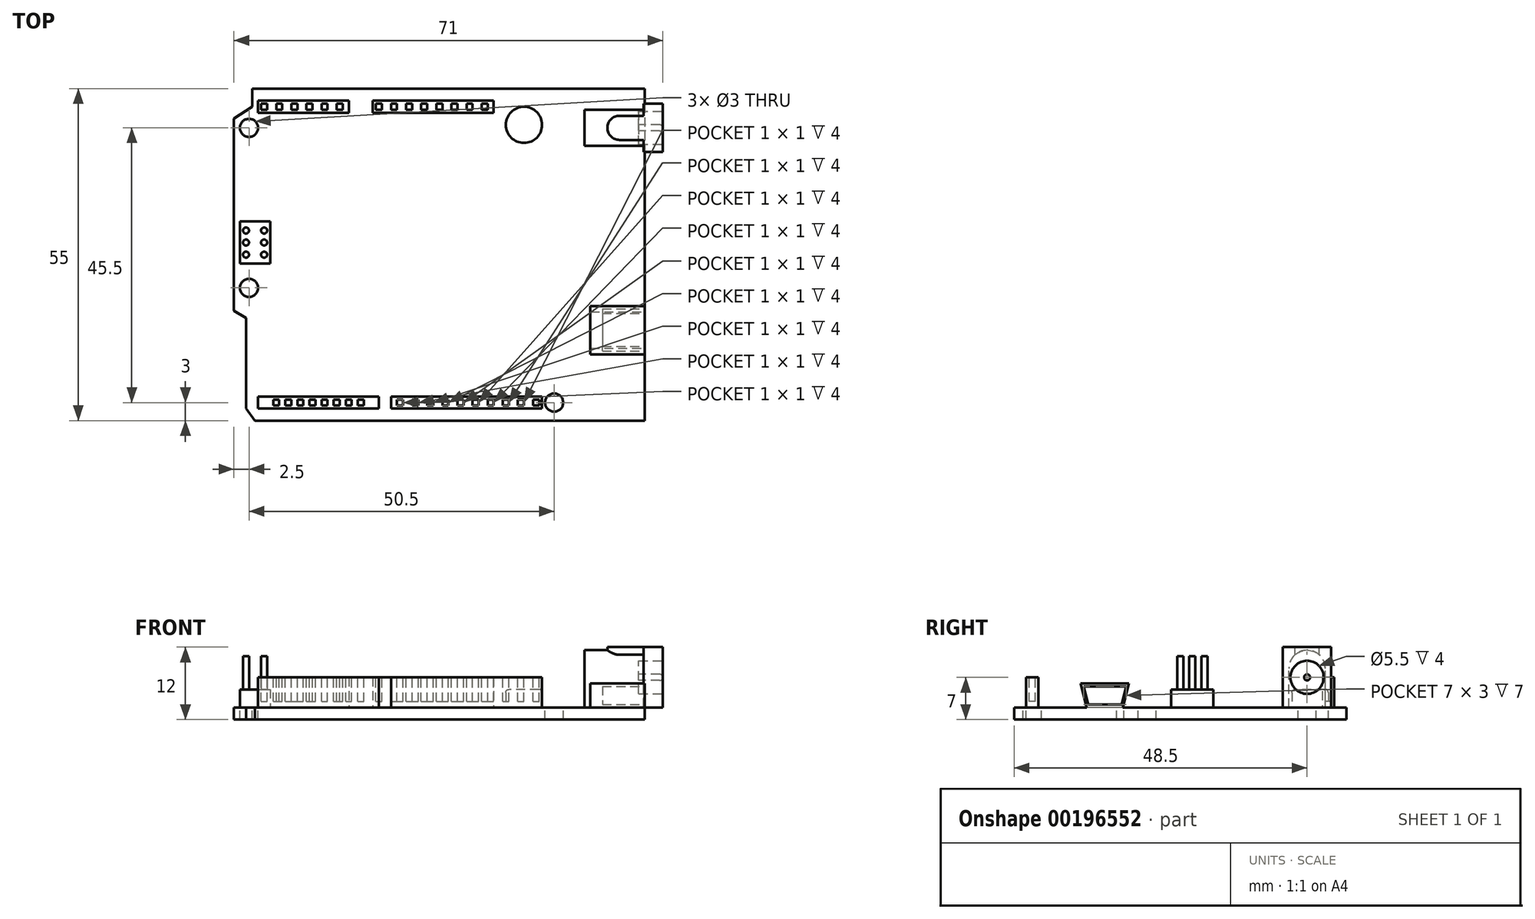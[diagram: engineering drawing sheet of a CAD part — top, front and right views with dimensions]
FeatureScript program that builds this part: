
annotation { "Feature Type Name" : "Feature", "Feature Type Description" : "" }
export const myFeature = defineFeature(function(context is Context, id is Id, definition is map)
    precondition{}
    {
        {
            var Q0;
            Q0=qCreatedBy(makeId("Top.planeOp"),FACE);
            var sketch = newSketch(context, id + "F0", { "sketchPlane" : qUnion([Q0])});
            skLineSegment(sketch, "E0.bottom", {"start": v(-34, 55) * mm, "end": v(34, 55) * mm});
            skLineSegment(sketch, "E0.top", {"start": v(-34, 0) * mm, "end": v(34, 0) * mm});
            skLineSegment(sketch, "E0.left", {"start": v(-34, 55) * mm, "end": v(-34, 0) * mm});
            skLineSegment(sketch, "E0.right", {"start": v(34, 55) * mm, "end": v(34, 0) * mm});
            skSolve(sketch);
        }
        {
            var Q0;
            Q0 = qSketchRegion(id + "F0", true);
            extrude(context, id + "F1", {"entities" : qUnion([Q0]), "depth" : 2 * mm});
        }
        {
            var Q0;
            Q0=makeQuery(id+"F1.opExtrude","CAP_FACE",FACE,{"disambiguationData":[OSD([sQuery(id+"F0.wireOp",EDGE,"E0.bottom"),sQuery(id+"F0.wireOp",EDGE,"E0.top"),sQuery(id+"F0.wireOp",EDGE,"E0.left"),sQuery(id+"F0.wireOp",EDGE,"E0.right")])],"isStart":false});
            var sketch = newSketch(context, id + "F2", { "sketchPlane" : qUnion([Q0])});
            skLineSegment(sketch, "E1.bottom", {"start": v(-34, 17) * mm, "end": v(-32, 17) * mm});
            skLineSegment(sketch, "E1.top", {"start": v(-34, 0) * mm, "end": v(-32, 0) * mm});
            skLineSegment(sketch, "E1.left", {"start": v(-34, 17) * mm, "end": v(-34, 0) * mm});
            skLineSegment(sketch, "E1.right", {"start": v(-32, 17) * mm, "end": v(-32, 0) * mm});
            skSolve(sketch);
        }
        {
            var Q0;
            Q0 = qSketchRegion(id + "F2", true);
            extrude(context, id + "F3", {"entities" : qUnion([Q0]), "operationType" : NewBodyOperationType.REMOVE, "endBound" : BoundingType.UP_TO_NEXT, "oppositeDirection" : true, "depth" : 25 * mm});
        }
        {
            var Q0;
            Q0=makeQuery(id+"F1.opExtrude","CAP_FACE",FACE,{"disambiguationData":[OSD([sQuery(id+"F0.wireOp",EDGE,"E0.bottom"),sQuery(id+"F0.wireOp",EDGE,"E0.top"),sQuery(id+"F0.wireOp",EDGE,"E0.left"),sQuery(id+"F0.wireOp",EDGE,"E0.right")])],"isStart":false});
            var sketch = newSketch(context, id + "F4", { "sketchPlane" : qUnion([Q0])});
            skLineSegment(sketch, "E2", {"start": v(-32, 2) * mm, "end": v(-30.5, 0) * mm});
            skLineSegment(sketch, "E3", {"start": v(-30.5, 0) * mm, "end": v(-32, 0) * mm});
            skLineSegment(sketch, "E4", {"start": v(-32, 0) * mm, "end": v(-32, 2) * mm});
            skSolve(sketch);
        }
        {
            var Q0;
            Q0 = qSketchRegion(id + "F4", true);
            extrude(context, id + "F5", {"entities" : qUnion([Q0]), "operationType" : NewBodyOperationType.REMOVE, "endBound" : BoundingType.UP_TO_NEXT, "oppositeDirection" : true, "depth" : 25 * mm});
        }
        {
            var Q0;
            Q0=makeQuery(id+"F1.opExtrude","CAP_FACE",FACE,{"disambiguationData":[OSD([sQuery(id+"F0.wireOp",EDGE,"E0.bottom"),sQuery(id+"F0.wireOp",EDGE,"E0.top"),sQuery(id+"F0.wireOp",EDGE,"E0.left"),sQuery(id+"F0.wireOp",EDGE,"E0.right")])],"isStart":false});
            var sketch = newSketch(context, id + "F6", { "sketchPlane" : qUnion([Q0])});
            skLineSegment(sketch, "E5", {"start": v(-34, 17) * mm, "end": v(-34, 18.2) * mm});
            skLineSegment(sketch, "E6", {"start": v(-34, 18.2) * mm, "end": v(-32, 17) * mm});
            skLineSegment(sketch, "E7", {"start": v(-32, 17) * mm, "end": v(-34, 17) * mm});
            skSolve(sketch);
        }
        {
            var Q0;
            Q0 = qSketchRegion(id + "F6", true);
            extrude(context, id + "F7", {"entities" : qUnion([Q0]), "operationType" : NewBodyOperationType.REMOVE, "endBound" : BoundingType.UP_TO_NEXT, "oppositeDirection" : true, "depth" : 25 * mm});
        }
        {
            var Q0;
            Q0=makeQuery(id+"F1.opExtrude","CAP_FACE",FACE,{"disambiguationData":[OSD([sQuery(id+"F0.wireOp",EDGE,"E0.bottom"),sQuery(id+"F0.wireOp",EDGE,"E0.top"),sQuery(id+"F0.wireOp",EDGE,"E0.left"),sQuery(id+"F0.wireOp",EDGE,"E0.right")])],"isStart":false});
            var sketch = newSketch(context, id + "F8", { "sketchPlane" : qUnion([Q0])});
            skLineSegment(sketch, "E8", {"start": v(-34, 50) * mm, "end": v(-34, 55) * mm});
            skLineSegment(sketch, "E9", {"start": v(-34, 55) * mm, "end": v(-31, 55) * mm});
            skLineSegment(sketch, "E10", {"start": v(-31, 55) * mm, "end": v(-31, 52) * mm});
            skLineSegment(sketch, "E11", {"start": v(-31, 52) * mm, "end": v(-34, 50) * mm});
            skSolve(sketch);
        }
        {
            var Q0;
            Q0 = qSketchRegion(id + "F8", true);
            extrude(context, id + "F9", {"entities" : qUnion([Q0]), "operationType" : NewBodyOperationType.REMOVE, "endBound" : BoundingType.UP_TO_NEXT, "oppositeDirection" : true, "depth" : 25 * mm});
        }
        {
            var Q0;
            Q0=makeQuery(id+"F1.opExtrude","CAP_FACE",FACE,{"disambiguationData":[OSD([sQuery(id+"F0.wireOp",EDGE,"E0.bottom"),sQuery(id+"F0.wireOp",EDGE,"E0.top"),sQuery(id+"F0.wireOp",EDGE,"E0.left"),sQuery(id+"F0.wireOp",EDGE,"E0.right")])],"isStart":false});
            var sketch = newSketch(context, id + "F10", { "sketchPlane" : qUnion([Q0])});
            skCircle(sketch, "E12", {"center": v(-31.5, 48.5) * mm, "radius": 1.5 * mm});
            skCircle(sketch, "E13", {"center": v(-31.5, 22) * mm, "radius": 1.5 * mm});
            skSolve(sketch);
        }
        {
            var Q0;
            Q0 = qSketchRegion(id + "F10", true);
            extrude(context, id + "F11", {"entities" : qUnion([Q0]), "operationType" : NewBodyOperationType.REMOVE, "endBound" : BoundingType.UP_TO_NEXT, "oppositeDirection" : true, "depth" : 25 * mm});
        }
        {
            var Q0;
            Q0=makeQuery(id+"F1.opExtrude","CAP_FACE",FACE,{"disambiguationData":[OSD([sQuery(id+"F0.wireOp",EDGE,"E0.bottom"),sQuery(id+"F0.wireOp",EDGE,"E0.top"),sQuery(id+"F0.wireOp",EDGE,"E0.left"),sQuery(id+"F0.wireOp",EDGE,"E0.right")])],"isStart":false});
            var sketch = newSketch(context, id + "F12", { "sketchPlane" : qUnion([Q0])});
            skCircle(sketch, "E14", {"center": v(19, 3) * mm, "radius": 1.5 * mm});
            skSolve(sketch);
        }
        {
            var Q0;
            Q0 = qSketchRegion(id + "F12", true);
            extrude(context, id + "F13", {"entities" : qUnion([Q0]), "operationType" : NewBodyOperationType.REMOVE, "endBound" : BoundingType.UP_TO_NEXT, "oppositeDirection" : true, "depth" : 25 * mm});
        }
        {
            var Q0;
            Q0=makeQuery(id+"F1.opExtrude","CAP_FACE",FACE,{"disambiguationData":[OSD([sQuery(id+"F0.wireOp",EDGE,"E0.bottom"),sQuery(id+"F0.wireOp",EDGE,"E0.top"),sQuery(id+"F0.wireOp",EDGE,"E0.left"),sQuery(id+"F0.wireOp",EDGE,"E0.right")])],"isStart":false});
            var sketch = newSketch(context, id + "F14", { "sketchPlane" : qUnion([Q0])});
            skLineSegment(sketch, "E15.bottom", {"start": v(-30, 53) * mm, "end": v(-15, 53) * mm});
            skLineSegment(sketch, "E15.top", {"start": v(-30, 51) * mm, "end": v(-15, 51) * mm});
            skLineSegment(sketch, "E15.left", {"start": v(-30, 53) * mm, "end": v(-30, 51) * mm});
            skLineSegment(sketch, "E15.right", {"start": v(-15, 53) * mm, "end": v(-15, 51) * mm});
            skSolve(sketch);
        }
        {
            var Q0;
            Q0 = qSketchRegion(id + "F14", true);
            extrude(context, id + "F15", {"entities" : qUnion([Q0]), "operationType" : NewBodyOperationType.ADD, "depth" : 5 * mm});
        }
        {
            var Q0;
            Q0=makeQuery(id+"F15.opExtrude","CAP_FACE",FACE,{"disambiguationData":[OSD([sQuery(id+"F14.wireOp",EDGE,"E15.bottom"),sQuery(id+"F14.wireOp",EDGE,"E15.top"),sQuery(id+"F14.wireOp",EDGE,"E15.left"),sQuery(id+"F14.wireOp",EDGE,"E15.right")])],"isStart":false});
            var sketch = newSketch(context, id + "F16", { "sketchPlane" : qUnion([Q0])});
            skPoint(sketch, "E16.oppositeSnap0", {"position": v(-30, 52) * mm});
            skLineSegment(sketch, "E17.bottom", {"start": v(-29.5, 52.5) * mm, "end": v(-28.5, 52.5) * mm});
            skLineSegment(sketch, "E17.top", {"start": v(-29.5, 51.5) * mm, "end": v(-28.5, 51.5) * mm});
            skLineSegment(sketch, "E17.left", {"start": v(-29.5, 52.5) * mm, "end": v(-29.5, 51.5) * mm});
            skLineSegment(sketch, "E17.right", {"start": v(-28.5, 52.5) * mm, "end": v(-28.5, 51.5) * mm});
            skSolve(sketch);
        }
        {
            var Q0;
            Q0 = qSketchRegion(id + "F16", true);
            extrude(context, id + "F17", {"entities" : qUnion([Q0]), "operationType" : NewBodyOperationType.REMOVE, "oppositeDirection" : true, "depth" : 4 * mm});
        }
        {
            var Q0;
            Q0=makeQuery(id+"F15.opExtrude","CAP_FACE",FACE,{"disambiguationData":[OSD([sQuery(id+"F14.wireOp",EDGE,"E15.bottom"),sQuery(id+"F14.wireOp",EDGE,"E15.top"),sQuery(id+"F14.wireOp",EDGE,"E15.left"),sQuery(id+"F14.wireOp",EDGE,"E15.right")])],"isStart":false});
            var sketch = newSketch(context, id + "F18", { "sketchPlane" : qUnion([Q0])});
            skLineSegment(sketch, "E18.bottom", {"start": v(-27, 52.5) * mm, "end": v(-26, 52.5) * mm});
            skLineSegment(sketch, "E18.top", {"start": v(-27, 51.5) * mm, "end": v(-26, 51.5) * mm});
            skLineSegment(sketch, "E18.left", {"start": v(-27, 52.5) * mm, "end": v(-27, 51.5) * mm});
            skLineSegment(sketch, "E18.right", {"start": v(-26, 52.5) * mm, "end": v(-26, 51.5) * mm});
            skLineSegment(sketch, "E19.bottom", {"start": v(-24.5, 52.5) * mm, "end": v(-23.5, 52.5) * mm});
            skLineSegment(sketch, "E19.top", {"start": v(-24.5, 51.5) * mm, "end": v(-23.5, 51.5) * mm});
            skLineSegment(sketch, "E19.left", {"start": v(-24.5, 52.5) * mm, "end": v(-24.5, 51.5) * mm});
            skLineSegment(sketch, "E19.right", {"start": v(-23.5, 52.5) * mm, "end": v(-23.5, 51.5) * mm});
            skLineSegment(sketch, "E20.bottom", {"start": v(-22, 52.5) * mm, "end": v(-21, 52.5) * mm});
            skLineSegment(sketch, "E20.top", {"start": v(-22, 51.5) * mm, "end": v(-21, 51.5) * mm});
            skLineSegment(sketch, "E20.left", {"start": v(-22, 52.5) * mm, "end": v(-22, 51.5) * mm});
            skLineSegment(sketch, "E20.right", {"start": v(-21, 52.5) * mm, "end": v(-21, 51.5) * mm});
            skLineSegment(sketch, "E21.bottom", {"start": v(-19.5, 52.5) * mm, "end": v(-18.5, 52.5) * mm});
            skLineSegment(sketch, "E21.top", {"start": v(-19.5, 51.5) * mm, "end": v(-18.5, 51.5) * mm});
            skLineSegment(sketch, "E21.left", {"start": v(-19.5, 52.5) * mm, "end": v(-19.5, 51.5) * mm});
            skLineSegment(sketch, "E21.right", {"start": v(-18.5, 52.5) * mm, "end": v(-18.5, 51.5) * mm});
            skLineSegment(sketch, "E22.bottom", {"start": v(-17, 52.5) * mm, "end": v(-16, 52.5) * mm});
            skLineSegment(sketch, "E22.top", {"start": v(-17, 51.5) * mm, "end": v(-16, 51.5) * mm});
            skLineSegment(sketch, "E22.left", {"start": v(-17, 52.5) * mm, "end": v(-17, 51.5) * mm});
            skLineSegment(sketch, "E22.right", {"start": v(-16, 52.5) * mm, "end": v(-16, 51.5) * mm});
            skSolve(sketch);
        }
        {
            var Q0;
            Q0 = qSketchRegion(id + "F18", true);
            extrude(context, id + "F19", {"entities" : qUnion([Q0]), "operationType" : NewBodyOperationType.REMOVE, "oppositeDirection" : true, "depth" : 4 * mm});
        }
        {
            var Q0;
            Q0=makeQuery(id+"F1.opExtrude","CAP_FACE",FACE,{"disambiguationData":[OSD([sQuery(id+"F0.wireOp",EDGE,"E0.bottom"),sQuery(id+"F0.wireOp",EDGE,"E0.top"),sQuery(id+"F0.wireOp",EDGE,"E0.left"),sQuery(id+"F0.wireOp",EDGE,"E0.right")])],"isStart":false});
            var sketch = newSketch(context, id + "F20", { "sketchPlane" : qUnion([Q0])});
            skLineSegment(sketch, "E23.bottom", {"start": v(-11, 53) * mm, "end": v(9, 53) * mm});
            skLineSegment(sketch, "E23.top", {"start": v(-11, 51) * mm, "end": v(9, 51) * mm});
            skLineSegment(sketch, "E23.left", {"start": v(-11, 53) * mm, "end": v(-11, 51) * mm});
            skLineSegment(sketch, "E23.right", {"start": v(9, 53) * mm, "end": v(9, 51) * mm});
            skSolve(sketch);
        }
        {
            var Q0;
            Q0 = qSketchRegion(id + "F20", true);
            extrude(context, id + "F21", {"entities" : qUnion([Q0]), "operationType" : NewBodyOperationType.ADD, "depth" : 5 * mm});
        }
        {
            var Q0;
            Q0=makeQuery(id+"F21.opExtrude","CAP_FACE",FACE,{"disambiguationData":[OSD([sQuery(id+"F20.wireOp",EDGE,"E23.bottom"),sQuery(id+"F20.wireOp",EDGE,"E23.top"),sQuery(id+"F20.wireOp",EDGE,"E23.left"),sQuery(id+"F20.wireOp",EDGE,"E23.right")])],"isStart":false});
            var sketch = newSketch(context, id + "F22", { "sketchPlane" : qUnion([Q0])});
            skLineSegment(sketch, "E24.bottom", {"start": v(-10.5, 52.5) * mm, "end": v(-9.5, 52.5) * mm});
            skLineSegment(sketch, "E24.top", {"start": v(-10.5, 51.5) * mm, "end": v(-9.5, 51.5) * mm});
            skLineSegment(sketch, "E24.left", {"start": v(-10.5, 52.5) * mm, "end": v(-10.5, 51.5) * mm});
            skLineSegment(sketch, "E24.right", {"start": v(-9.5, 52.5) * mm, "end": v(-9.5, 51.5) * mm});
            skLineSegment(sketch, "E25.bottom", {"start": v(-8, 52.5) * mm, "end": v(-7, 52.5) * mm});
            skLineSegment(sketch, "E25.top", {"start": v(-8, 51.5) * mm, "end": v(-7, 51.5) * mm});
            skLineSegment(sketch, "E25.left", {"start": v(-8, 52.5) * mm, "end": v(-8, 51.5) * mm});
            skLineSegment(sketch, "E25.right", {"start": v(-7, 52.5) * mm, "end": v(-7, 51.5) * mm});
            skLineSegment(sketch, "E26.bottom", {"start": v(-5.5, 52.5) * mm, "end": v(-4.5, 52.5) * mm});
            skLineSegment(sketch, "E26.top", {"start": v(-5.5, 51.5) * mm, "end": v(-4.5, 51.5) * mm});
            skLineSegment(sketch, "E26.left", {"start": v(-5.5, 52.5) * mm, "end": v(-5.5, 51.5) * mm});
            skLineSegment(sketch, "E26.right", {"start": v(-4.5, 52.5) * mm, "end": v(-4.5, 51.5) * mm});
            skLineSegment(sketch, "E27.bottom", {"start": v(-3, 52.5) * mm, "end": v(-2, 52.5) * mm});
            skLineSegment(sketch, "E27.top", {"start": v(-3, 51.5) * mm, "end": v(-2, 51.5) * mm});
            skLineSegment(sketch, "E27.left", {"start": v(-3, 52.5) * mm, "end": v(-3, 51.5) * mm});
            skLineSegment(sketch, "E27.right", {"start": v(-2, 52.5) * mm, "end": v(-2, 51.5) * mm});
            skLineSegment(sketch, "E28.bottom", {"start": v(-0.5, 52.5) * mm, "end": v(0.5, 52.5) * mm});
            skLineSegment(sketch, "E28.top", {"start": v(-0.5, 51.5) * mm, "end": v(0.5, 51.5) * mm});
            skLineSegment(sketch, "E28.left", {"start": v(-0.5, 52.5) * mm, "end": v(-0.5, 51.5) * mm});
            skLineSegment(sketch, "E28.right", {"start": v(0.5, 52.5) * mm, "end": v(0.5, 51.5) * mm});
            skLineSegment(sketch, "E29.bottom", {"start": v(2, 52.5) * mm, "end": v(3, 52.5) * mm});
            skLineSegment(sketch, "E29.top", {"start": v(2, 51.5) * mm, "end": v(3, 51.5) * mm});
            skLineSegment(sketch, "E29.left", {"start": v(2, 52.5) * mm, "end": v(2, 51.5) * mm});
            skLineSegment(sketch, "E29.right", {"start": v(3, 52.5) * mm, "end": v(3, 51.5) * mm});
            skLineSegment(sketch, "E30.bottom", {"start": v(4.5, 52.5) * mm, "end": v(5.5, 52.5) * mm});
            skLineSegment(sketch, "E30.top", {"start": v(4.5, 51.5) * mm, "end": v(5.5, 51.5) * mm});
            skLineSegment(sketch, "E30.left", {"start": v(4.5, 52.5) * mm, "end": v(4.5, 51.5) * mm});
            skLineSegment(sketch, "E30.right", {"start": v(5.5, 52.5) * mm, "end": v(5.5, 51.5) * mm});
            skLineSegment(sketch, "E31.bottom", {"start": v(7, 52.5) * mm, "end": v(8, 52.5) * mm});
            skLineSegment(sketch, "E31.top", {"start": v(7, 51.5) * mm, "end": v(8, 51.5) * mm});
            skLineSegment(sketch, "E31.left", {"start": v(7, 52.5) * mm, "end": v(7, 51.5) * mm});
            skLineSegment(sketch, "E31.right", {"start": v(8, 52.5) * mm, "end": v(8, 51.5) * mm});
            skSolve(sketch);
        }
        {
            var Q0;
            Q0 = qSketchRegion(id + "F22", true);
            extrude(context, id + "F23", {"entities" : qUnion([Q0]), "operationType" : NewBodyOperationType.REMOVE, "oppositeDirection" : true, "depth" : 4 * mm});
        }
        {
            var Q0;
            Q0=makeQuery(id+"F1.opExtrude","CAP_FACE",FACE,{"disambiguationData":[OSD([sQuery(id+"F0.wireOp",EDGE,"E0.bottom"),sQuery(id+"F0.wireOp",EDGE,"E0.top"),sQuery(id+"F0.wireOp",EDGE,"E0.left"),sQuery(id+"F0.wireOp",EDGE,"E0.right")])],"isStart":false});
            var sketch = newSketch(context, id + "F24", { "sketchPlane" : qUnion([Q0])});
            skLineSegment(sketch, "E32.bottom", {"start": v(-30, 4) * mm, "end": v(-10, 4) * mm});
            skLineSegment(sketch, "E32.top", {"start": v(-30, 2) * mm, "end": v(-10, 2) * mm});
            skLineSegment(sketch, "E32.left", {"start": v(-30, 4) * mm, "end": v(-30, 2) * mm});
            skLineSegment(sketch, "E32.right", {"start": v(-10, 4) * mm, "end": v(-10, 2) * mm});
            skLineSegment(sketch, "E33.bottom", {"start": v(-8, 4) * mm, "end": v(17, 4) * mm});
            skLineSegment(sketch, "E33.top", {"start": v(-8, 2) * mm, "end": v(17, 2) * mm});
            skLineSegment(sketch, "E33.left", {"start": v(-8, 4) * mm, "end": v(-8, 2) * mm});
            skLineSegment(sketch, "E33.right", {"start": v(17, 4) * mm, "end": v(17, 2) * mm});
            skSolve(sketch);
        }
        {
            var Q0;
            Q0 = qSketchRegion(id + "F24", true);
            extrude(context, id + "F25", {"entities" : qUnion([Q0]), "operationType" : NewBodyOperationType.ADD, "depth" : 5 * mm});
        }
        {
            var Q0;
            Q0=makeQuery(id+"F25.opExtrude","CAP_FACE",FACE,{"disambiguationData":[OSD([sQuery(id+"F24.wireOp",EDGE,"E32.bottom"),sQuery(id+"F24.wireOp",EDGE,"E32.top"),sQuery(id+"F24.wireOp",EDGE,"E32.left"),sQuery(id+"F24.wireOp",EDGE,"E32.right")])],"isStart":false});
            var sketch = newSketch(context, id + "F26", { "sketchPlane" : qUnion([Q0])});
            skLineSegment(sketch, "E34.bottom", {"start": v(-27.5, 3.5) * mm, "end": v(-26.5, 3.5) * mm});
            skLineSegment(sketch, "E34.top", {"start": v(-27.5, 2.5) * mm, "end": v(-26.5, 2.5) * mm});
            skLineSegment(sketch, "E34.left", {"start": v(-27.5, 3.5) * mm, "end": v(-27.5, 2.5) * mm});
            skLineSegment(sketch, "E34.right", {"start": v(-26.5, 3.5) * mm, "end": v(-26.5, 2.5) * mm});
            skLineSegment(sketch, "E35.bottom", {"start": v(-25.5, 3.5) * mm, "end": v(-24.5, 3.5) * mm});
            skLineSegment(sketch, "E35.top", {"start": v(-25.5, 2.5) * mm, "end": v(-24.5, 2.5) * mm});
            skLineSegment(sketch, "E35.left", {"start": v(-25.5, 3.5) * mm, "end": v(-25.5, 2.5) * mm});
            skLineSegment(sketch, "E35.right", {"start": v(-24.5, 3.5) * mm, "end": v(-24.5, 2.5) * mm});
            skLineSegment(sketch, "E36.bottom", {"start": v(-23.5, 3.5) * mm, "end": v(-22.5, 3.5) * mm});
            skLineSegment(sketch, "E36.top", {"start": v(-23.5, 2.5) * mm, "end": v(-22.5, 2.5) * mm});
            skLineSegment(sketch, "E36.left", {"start": v(-23.5, 3.5) * mm, "end": v(-23.5, 2.5) * mm});
            skLineSegment(sketch, "E36.right", {"start": v(-22.5, 3.5) * mm, "end": v(-22.5, 2.5) * mm});
            skLineSegment(sketch, "E37.bottom", {"start": v(-21.5, 3.5) * mm, "end": v(-20.5, 3.5) * mm});
            skLineSegment(sketch, "E37.top", {"start": v(-21.5, 2.5) * mm, "end": v(-20.5, 2.5) * mm});
            skLineSegment(sketch, "E37.left", {"start": v(-21.5, 3.5) * mm, "end": v(-21.5, 2.5) * mm});
            skLineSegment(sketch, "E37.right", {"start": v(-20.5, 3.5) * mm, "end": v(-20.5, 2.5) * mm});
            skLineSegment(sketch, "E38.bottom", {"start": v(-19.5, 3.5) * mm, "end": v(-18.5, 3.5) * mm});
            skLineSegment(sketch, "E38.top", {"start": v(-19.5, 2.5) * mm, "end": v(-18.5, 2.5) * mm});
            skLineSegment(sketch, "E38.left", {"start": v(-19.5, 3.5) * mm, "end": v(-19.5, 2.5) * mm});
            skLineSegment(sketch, "E38.right", {"start": v(-18.5, 3.5) * mm, "end": v(-18.5, 2.5) * mm});
            skLineSegment(sketch, "E39.bottom", {"start": v(-17.5, 3.5) * mm, "end": v(-16.5, 3.5) * mm});
            skLineSegment(sketch, "E39.top", {"start": v(-17.5, 2.5) * mm, "end": v(-16.5, 2.5) * mm});
            skLineSegment(sketch, "E39.left", {"start": v(-17.5, 3.5) * mm, "end": v(-17.5, 2.5) * mm});
            skLineSegment(sketch, "E39.right", {"start": v(-16.5, 3.5) * mm, "end": v(-16.5, 2.5) * mm});
            skLineSegment(sketch, "E40.bottom", {"start": v(-15.5, 3.5) * mm, "end": v(-14.5, 3.5) * mm});
            skLineSegment(sketch, "E40.top", {"start": v(-15.5, 2.5) * mm, "end": v(-14.5, 2.5) * mm});
            skLineSegment(sketch, "E40.left", {"start": v(-15.5, 3.5) * mm, "end": v(-15.5, 2.5) * mm});
            skLineSegment(sketch, "E40.right", {"start": v(-14.5, 3.5) * mm, "end": v(-14.5, 2.5) * mm});
            skLineSegment(sketch, "E41.bottom", {"start": v(-13.5, 3.5) * mm, "end": v(-12.5, 3.5) * mm});
            skLineSegment(sketch, "E41.top", {"start": v(-13.5, 2.5) * mm, "end": v(-12.5, 2.5) * mm});
            skLineSegment(sketch, "E41.left", {"start": v(-13.5, 3.5) * mm, "end": v(-13.5, 2.5) * mm});
            skLineSegment(sketch, "E41.right", {"start": v(-12.5, 3.5) * mm, "end": v(-12.5, 2.5) * mm});
            skSolve(sketch);
        }
        {
            var Q0;
            Q0 = qSketchRegion(id + "F26", true);
            extrude(context, id + "F27", {"entities" : qUnion([Q0]), "operationType" : NewBodyOperationType.REMOVE, "oppositeDirection" : true, "depth" : 4 * mm});
        }
        {
            var Q0;
            Q0=makeQuery(id+"F25.opExtrude","CAP_FACE",FACE,{"disambiguationData":[OSD([sQuery(id+"F24.wireOp",EDGE,"E33.bottom"),sQuery(id+"F24.wireOp",EDGE,"E33.top"),sQuery(id+"F24.wireOp",EDGE,"E33.left"),sQuery(id+"F24.wireOp",EDGE,"E33.right")])],"isStart":false});
            var sketch = newSketch(context, id + "F28", { "sketchPlane" : qUnion([Q0])});
            skLineSegment(sketch, "E42.bottom", {"start": v(-7, 3.5) * mm, "end": v(-6, 3.5) * mm});
            skLineSegment(sketch, "E42.top", {"start": v(-7, 2.5) * mm, "end": v(-6, 2.5) * mm});
            skLineSegment(sketch, "E42.left", {"start": v(-7, 3.5) * mm, "end": v(-7, 2.5) * mm});
            skLineSegment(sketch, "E42.right", {"start": v(-6, 3.5) * mm, "end": v(-6, 2.5) * mm});
            skLineSegment(sketch, "E43.bottom", {"start": v(-4.5, 3.5) * mm, "end": v(-3.5, 3.5) * mm});
            skLineSegment(sketch, "E43.top", {"start": v(-4.5, 2.5) * mm, "end": v(-3.5, 2.5) * mm});
            skLineSegment(sketch, "E43.left", {"start": v(-4.5, 3.5) * mm, "end": v(-4.5, 2.5) * mm});
            skLineSegment(sketch, "E43.right", {"start": v(-3.5, 3.5) * mm, "end": v(-3.5, 2.5) * mm});
            skLineSegment(sketch, "E44.bottom", {"start": v(-2, 3.5) * mm, "end": v(-1, 3.5) * mm});
            skLineSegment(sketch, "E44.top", {"start": v(-2, 2.5) * mm, "end": v(-1, 2.5) * mm});
            skLineSegment(sketch, "E44.left", {"start": v(-2, 3.5) * mm, "end": v(-2, 2.5) * mm});
            skLineSegment(sketch, "E44.right", {"start": v(-1, 3.5) * mm, "end": v(-1, 2.5) * mm});
            skLineSegment(sketch, "E45.bottom", {"start": v(0.5, 3.5) * mm, "end": v(1.5, 3.5) * mm});
            skLineSegment(sketch, "E45.top", {"start": v(0.5, 2.5) * mm, "end": v(1.5, 2.5) * mm});
            skLineSegment(sketch, "E45.left", {"start": v(0.5, 3.5) * mm, "end": v(0.5, 2.5) * mm});
            skLineSegment(sketch, "E45.right", {"start": v(1.5, 3.5) * mm, "end": v(1.5, 2.5) * mm});
            skLineSegment(sketch, "E46.bottom", {"start": v(3, 3.5) * mm, "end": v(4, 3.5) * mm});
            skLineSegment(sketch, "E46.top", {"start": v(3, 2.5) * mm, "end": v(4, 2.5) * mm});
            skLineSegment(sketch, "E46.left", {"start": v(3, 3.5) * mm, "end": v(3, 2.5) * mm});
            skLineSegment(sketch, "E46.right", {"start": v(4, 3.5) * mm, "end": v(4, 2.5) * mm});
            skLineSegment(sketch, "E47.bottom", {"start": v(8, 3.5) * mm, "end": v(9, 3.5) * mm});
            skLineSegment(sketch, "E47.top", {"start": v(8, 2.5) * mm, "end": v(9, 2.5) * mm});
            skLineSegment(sketch, "E47.left", {"start": v(8, 3.5) * mm, "end": v(8, 2.5) * mm});
            skLineSegment(sketch, "E47.right", {"start": v(9, 3.5) * mm, "end": v(9, 2.5) * mm});
            skLineSegment(sketch, "E48.bottom", {"start": v(5.5, 3.5) * mm, "end": v(6.5, 3.5) * mm});
            skLineSegment(sketch, "E48.top", {"start": v(5.5, 2.5) * mm, "end": v(6.5, 2.5) * mm});
            skLineSegment(sketch, "E48.left", {"start": v(5.5, 3.5) * mm, "end": v(5.5, 2.5) * mm});
            skLineSegment(sketch, "E48.right", {"start": v(6.5, 3.5) * mm, "end": v(6.5, 2.5) * mm});
            skLineSegment(sketch, "E49.bottom", {"start": v(10.5, 3.5) * mm, "end": v(11.5, 3.5) * mm});
            skLineSegment(sketch, "E49.top", {"start": v(10.5, 2.5) * mm, "end": v(11.5, 2.5) * mm});
            skLineSegment(sketch, "E49.left", {"start": v(10.5, 3.5) * mm, "end": v(10.5, 2.5) * mm});
            skLineSegment(sketch, "E49.right", {"start": v(11.5, 3.5) * mm, "end": v(11.5, 2.5) * mm});
            skLineSegment(sketch, "E50.bottom", {"start": v(13, 3.5) * mm, "end": v(14, 3.5) * mm});
            skLineSegment(sketch, "E50.top", {"start": v(13, 2.5) * mm, "end": v(14, 2.5) * mm});
            skLineSegment(sketch, "E50.left", {"start": v(13, 3.5) * mm, "end": v(13, 2.5) * mm});
            skLineSegment(sketch, "E50.right", {"start": v(14, 3.5) * mm, "end": v(14, 2.5) * mm});
            skLineSegment(sketch, "E51.bottom", {"start": v(15.5, 3.5) * mm, "end": v(16.5, 3.5) * mm});
            skLineSegment(sketch, "E51.top", {"start": v(15.5, 2.5) * mm, "end": v(16.5, 2.5) * mm});
            skLineSegment(sketch, "E51.left", {"start": v(15.5, 3.5) * mm, "end": v(15.5, 2.5) * mm});
            skLineSegment(sketch, "E51.right", {"start": v(16.5, 3.5) * mm, "end": v(16.5, 2.5) * mm});
            skSolve(sketch);
        }
        {
            var Q0;
            Q0 = qSketchRegion(id + "F28", true);
            extrude(context, id + "F29", {"entities" : qUnion([Q0]), "operationType" : NewBodyOperationType.REMOVE, "oppositeDirection" : true, "depth" : 4 * mm});
        }
        {
            var Q0;
            Q0=makeQuery(id+"F1.opExtrude","CAP_FACE",FACE,{"disambiguationData":[OSD([sQuery(id+"F0.wireOp",EDGE,"E0.bottom"),sQuery(id+"F0.wireOp",EDGE,"E0.top"),sQuery(id+"F0.wireOp",EDGE,"E0.left"),sQuery(id+"F0.wireOp",EDGE,"E0.right")])],"isStart":false});
            var sketch = newSketch(context, id + "F30", { "sketchPlane" : qUnion([Q0])});
            skCircle(sketch, "E52", {"center": v(14, 49) * mm, "radius": 3 * mm});
            skSolve(sketch);
        }
        {
            var Q0;
            Q0 = qSketchRegion(id + "F30", true);
            extrude(context, id + "F31", {"entities" : qUnion([Q0]), "operationType" : NewBodyOperationType.ADD, "depth" : 3 * mm});
        }
        {
            var Q0;
            Q0=makeQuery(id+"F31.opExtrude","CAP_EDGE",EDGE,{"disambiguationData":[OSD([sQuery(id+"F30.wireOp",EDGE,"E52")])],"isStart":false});
            fillet(context, id + "F32", {"entities" : qUnion([Q0]), "radius" : 0.5 * mm, "tangentPropagation" : true, "allowEdgeOverflow" : false});
        }
        {
            var Q0;
            Q0=makeQuery(id+"F1.opExtrude","CAP_FACE",FACE,{"disambiguationData":[OSD([sQuery(id+"F0.wireOp",EDGE,"E0.bottom"),sQuery(id+"F0.wireOp",EDGE,"E0.top"),sQuery(id+"F0.wireOp",EDGE,"E0.left"),sQuery(id+"F0.wireOp",EDGE,"E0.right")])],"isStart":false});
            var sketch = newSketch(context, id + "F33", { "sketchPlane" : qUnion([Q0])});
            skLineSegment(sketch, "E53.bottom", {"start": v(-33, 33) * mm, "end": v(-28, 33) * mm});
            skLineSegment(sketch, "E53.top", {"start": v(-33, 26) * mm, "end": v(-28, 26) * mm});
            skLineSegment(sketch, "E53.left", {"start": v(-33, 33) * mm, "end": v(-33, 26) * mm});
            skLineSegment(sketch, "E53.right", {"start": v(-28, 33) * mm, "end": v(-28, 26) * mm});
            skSolve(sketch);
        }
        {
            var Q0;
            Q0 = qSketchRegion(id + "F33", true);
            extrude(context, id + "F34", {"entities" : qUnion([Q0]), "operationType" : NewBodyOperationType.ADD, "depth" : 3 * mm});
        }
        {
            var Q0;
            Q0=makeQuery(id+"F34.opExtrude","CAP_FACE",FACE,{"disambiguationData":[OSD([sQuery(id+"F33.wireOp",EDGE,"E53.bottom"),sQuery(id+"F33.wireOp",EDGE,"E53.top"),sQuery(id+"F33.wireOp",EDGE,"E53.left"),sQuery(id+"F33.wireOp",EDGE,"E53.right")])],"isStart":false});
            var sketch = newSketch(context, id + "F35", { "sketchPlane" : qUnion([Q0])});
            skCircle(sketch, "E54", {"center": v(-32, 31.5) * mm, "radius": 0.5 * mm});
            skCircle(sketch, "E55", {"center": v(-32, 29.5) * mm, "radius": 0.5 * mm});
            skCircle(sketch, "E56", {"center": v(-32, 27.5) * mm, "radius": 0.5 * mm});
            skCircle(sketch, "E57", {"center": v(-29, 31.5) * mm, "radius": 0.5 * mm});
            skCircle(sketch, "E58", {"center": v(-29, 29.5) * mm, "radius": 0.5 * mm});
            skCircle(sketch, "E59", {"center": v(-29, 27.5) * mm, "radius": 0.5 * mm});
            skSolve(sketch);
        }
        {
            var Q0;
            Q0 = qSketchRegion(id + "F35", true);
            extrude(context, id + "F36", {"entities" : qUnion([Q0]), "operationType" : NewBodyOperationType.ADD, "depth" : 5.5 * mm});
        }
        {
            var Q0;
            Q0=makeQuery(id+"F1.opExtrude","SWEPT_FACE",FACE,{"disambiguationData":[OSD([sQuery(id+"F0.wireOp",EDGE,"E0.right")])]});
            var sketch = newSketch(context, id + "F37", { "sketchPlane" : qUnion([Q0])});
            skLineSegment(sketch, "E60", {"start": v(18, 2) * mm, "end": v(12, 2) * mm});
            skLineSegment(sketch, "E61", {"start": v(19, 6) * mm, "end": v(11, 6) * mm});
            skLineSegment(sketch, "E62", {"start": v(19, 6) * mm, "end": v(18, 2) * mm});
            skLineSegment(sketch, "E63", {"start": v(11, 6) * mm, "end": v(12, 2) * mm});
            skSolve(sketch);
        }
        {
            var Q0;
            Q0 = qSketchRegion(id + "F37", true);
            extrude(context, id + "F38", {"entities" : qUnion([Q0]), "operationType" : NewBodyOperationType.ADD, "oppositeDirection" : true, "depth" : 9 * mm});
        }
        {
            var Q0;
            Q0=makeQuery(id+"F38.boolean.opBoolean","MERGE",FACE,{"derivedFrom":[makeQuery(id+"F1.opExtrude","SWEPT_FACE",FACE,{"disambiguationData":[OSD([sQuery(id+"F0.wireOp",EDGE,"E0.right")])]}),makeQuery(id+"F38.opExtrude","CAP_FACE",FACE,{"disambiguationData":[OSD([sQuery(id+"F37.wireOp",EDGE,"E60"),sQuery(id+"F37.wireOp",EDGE,"E61"),sQuery(id+"F37.wireOp",EDGE,"E62"),sQuery(id+"F37.wireOp",EDGE,"E63")])],"isStart":true})]});
            var sketch = newSketch(context, id + "F39", { "sketchPlane" : qUnion([Q0])});
            skLineSegment(sketch, "E64", {"start": v(18.54, 5.5) * mm, "end": v(11.54, 5.5) * mm});
            skLineSegment(sketch, "E65", {"start": v(17.79, 2.5) * mm, "end": v(12.29, 2.5) * mm});
            skLineSegment(sketch, "E66", {"start": v(11.54, 5.5) * mm, "end": v(12.29, 2.5) * mm});
            skLineSegment(sketch, "E67", {"start": v(18.54, 5.5) * mm, "end": v(17.79, 2.5) * mm});
            skSolve(sketch);
        }
        {
            var Q0;
            Q0 = qSketchRegion(id + "F39", true);
            extrude(context, id + "F40", {"entities" : qUnion([Q0]), "operationType" : NewBodyOperationType.REMOVE, "oppositeDirection" : true, "depth" : 7 * mm});
        }
        {
            var Q0;
            Q0=makeQuery(id+"F1.opExtrude","CAP_FACE",FACE,{"disambiguationData":[OSD([sQuery(id+"F0.wireOp",EDGE,"E0.bottom"),sQuery(id+"F0.wireOp",EDGE,"E0.top"),sQuery(id+"F0.wireOp",EDGE,"E0.left"),sQuery(id+"F0.wireOp",EDGE,"E0.right")])],"isStart":false});
            var sketch = newSketch(context, id + "F41", { "sketchPlane" : qUnion([Q0])});
            skLineSegment(sketch, "E68.bottom", {"start": v(33.8, 52.5) * mm, "end": v(37, 52.5) * mm});
            skLineSegment(sketch, "E68.top", {"start": v(33.8, 44.5) * mm, "end": v(37, 44.5) * mm});
            skLineSegment(sketch, "E68.left", {"start": v(33.8, 52.5) * mm, "end": v(33.8, 44.5) * mm});
            skLineSegment(sketch, "E68.right", {"start": v(37, 52.5) * mm, "end": v(37, 44.5) * mm});
            skSolve(sketch);
        }
        {
            var Q0;
            Q0 = qSketchRegion(id + "F41", true);
            extrude(context, id + "F42", {"entities" : qUnion([Q0]), "operationType" : NewBodyOperationType.ADD, "depth" : 10 * mm});
        }
        {
            var Q0;
            Q0=makeQuery(id+"F42.opExtrude","SWEPT_FACE",FACE,{"disambiguationData":[OSD([sQuery(id+"F41.wireOp",EDGE,"E68.right")])]});
            var sketch = newSketch(context, id + "F43", { "sketchPlane" : qUnion([Q0])});
            skLineSegment(sketch, "E69", {"start": v(51.5, 2) * mm, "end": v(51.5, 8.5) * mm});
            skLineSegment(sketch, "E70", {"start": v(51.5, 2) * mm, "end": v(45.5, 2) * mm});
            skLineSegment(sketch, "E71", {"start": v(45.5, 2) * mm, "end": v(45.5, 8.5) * mm});
            skArc(sketch, "E72", {"start": v(51.5, 8.5) * mm, "mid": v(48.5, 11.5) * mm, "end": v(45.5, 8.5) * mm});
            skSolve(sketch);
        }
        {
            var Q0;
            Q0 = qSketchRegion(id + "F43", true);
            extrude(context, id + "F44", {"entities" : qUnion([Q0]), "operationType" : NewBodyOperationType.ADD, "oppositeDirection" : true, "depth" : 13 * mm});
        }
        {
            var Q0;
            Q0=makeQuery(id+"F42.opExtrude","CAP_FACE",FACE,{"disambiguationData":[OSD([sQuery(id+"F41.wireOp",EDGE,"E68.bottom"),sQuery(id+"F41.wireOp",EDGE,"E68.top"),sQuery(id+"F41.wireOp",EDGE,"E68.left"),sQuery(id+"F41.wireOp",EDGE,"E68.right")])],"isStart":false});
            var sketch = newSketch(context, id + "F45", { "sketchPlane" : qUnion([Q0])});
            skLineSegment(sketch, "E73", {"start": v(33.8, 46.5) * mm, "end": v(29.8, 46.5) * mm});
            skLineSegment(sketch, "E74", {"start": v(33.8, 50.5) * mm, "end": v(29.8, 50.5) * mm});
            skLineSegment(sketch, "E75", {"start": v(33.8, 46.5) * mm, "end": v(33.8, 50.5) * mm});
            skArc(sketch, "E76", {"start": v(29.8, 50.5) * mm, "mid": v(27.8, 48.5) * mm, "end": v(29.8, 46.5) * mm});
            skSolve(sketch);
        }
        {
            var Q0;
            Q0 = qSketchRegion(id + "F45", true);
            extrude(context, id + "F46", {"entities" : qUnion([Q0]), "operationType" : NewBodyOperationType.ADD, "endBound" : BoundingType.UP_TO_NEXT, "oppositeDirection" : true, "depth" : 25 * mm});
        }
        {
            var Q0;
            Q0=makeQuery(id+"F42.opExtrude","SWEPT_FACE",FACE,{"disambiguationData":[OSD([sQuery(id+"F41.wireOp",EDGE,"E68.right")])]});
            var sketch = newSketch(context, id + "F47", { "sketchPlane" : qUnion([Q0])});
            skCircle(sketch, "E77", {"center": v(48.5, 7) * mm, "radius": 2.75 * mm});
            skSolve(sketch);
        }
        {
            var Q0;
            Q0 = qSketchRegion(id + "F47", true);
            extrude(context, id + "F48", {"entities" : qUnion([Q0]), "operationType" : NewBodyOperationType.REMOVE, "oppositeDirection" : true, "depth" : 4 * mm});
        }
        {
            var Q0;
            Q0=makeQuery(id+"F48.boolean.opBoolean","COPY",FACE,{"derivedFrom":makeQuery(id+"F48.opExtrude","CAP_FACE",FACE,{"disambiguationData":[OSD([sQuery(id+"F47.wireOp",EDGE,"E77")])],"isStart":false})});
            var sketch = newSketch(context, id + "F49", { "sketchPlane" : qUnion([Q0])});
            skCircle(sketch, "E78", {"center": v(48.5, 7) * mm, "radius": 0.5 * mm});
            skSolve(sketch);
        }
        {
            var Q0;
            Q0 = qSketchRegion(id + "F49", true);
            extrude(context, id + "F50", {"entities" : qUnion([Q0]), "operationType" : NewBodyOperationType.ADD, "depth" : 4 * mm});
        }
        {
            var Q0;
            Q0=makeQuery(id+"F50.opExtrude","CAP_FACE",FACE,{"disambiguationData":[OSD([sQuery(id+"F49.wireOp",EDGE,"E78")])],"isStart":false});
            fillet(context, id + "F51", {"entities" : qUnion([Q0]), "radius" : 0.5 * mm, "tangentPropagation" : true, "allowEdgeOverflow" : false});
        }
    });
